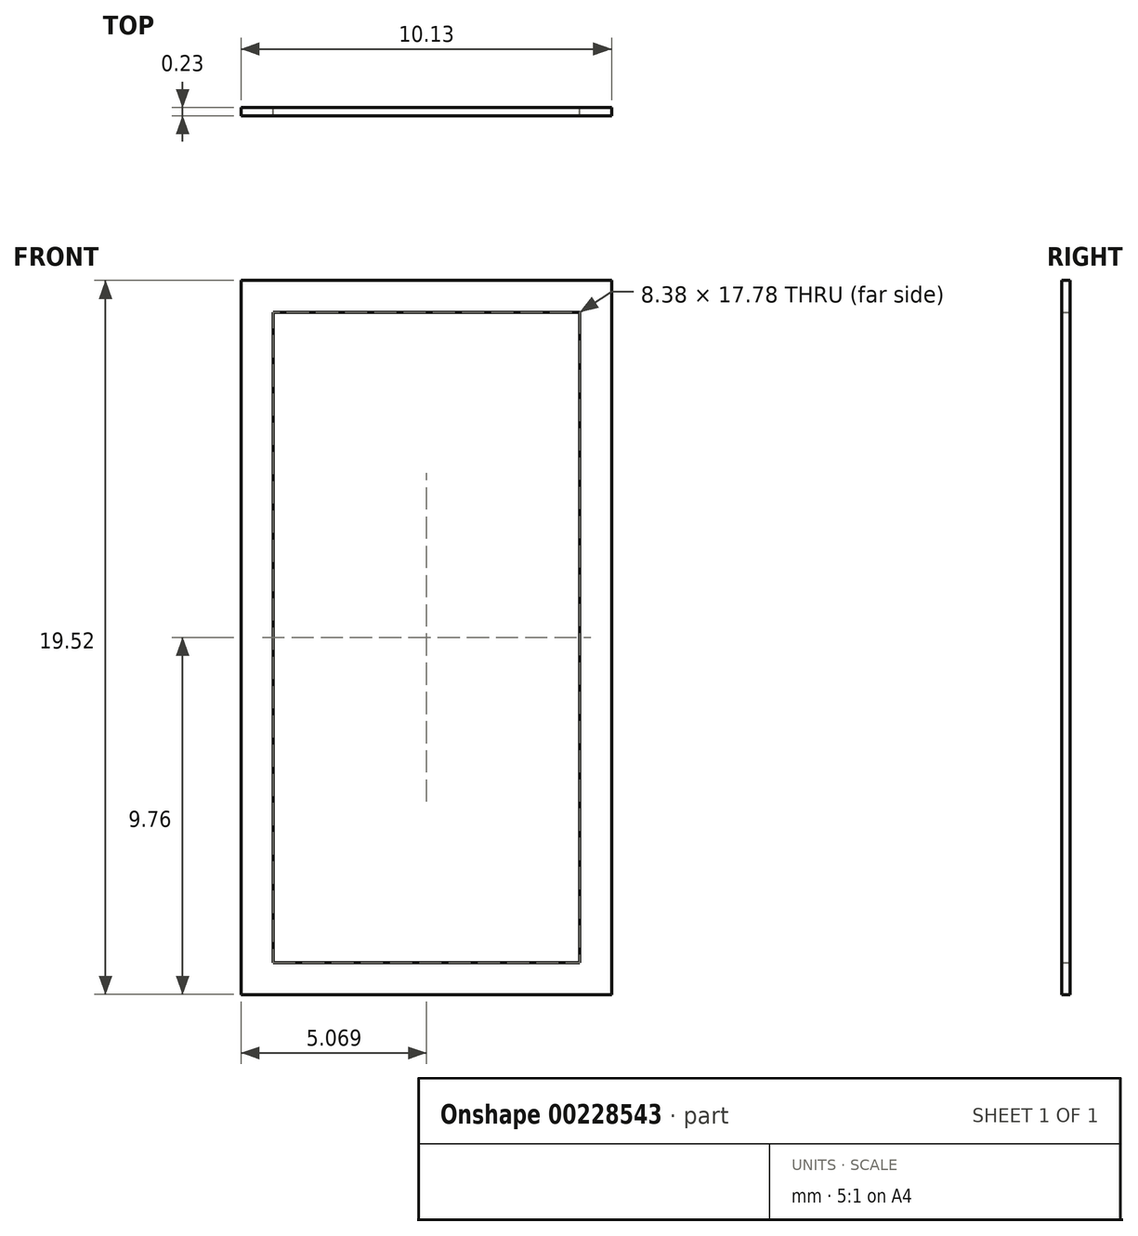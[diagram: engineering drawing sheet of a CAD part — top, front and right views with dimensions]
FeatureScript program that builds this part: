
annotation { "Feature Type Name" : "Feature", "Feature Type Description" : "" }
export const myFeature = defineFeature(function(context is Context, id is Id, definition is map)
    precondition{}
    {
        {
            var Q0;
            Q0=qCreatedBy(makeId("Front.planeOp"),FACE);
            var sketch = newSketch(context, id + "F0", { "sketchPlane" : qUnion([Q0])});
            skLineSegment(sketch, "E0.bottom", {"start": v(0, 0) * mm, "end": v(-8.38, 0) * mm});
            skLineSegment(sketch, "E0.top", {"start": v(0, 17.78) * mm, "end": v(-8.38, 17.78) * mm});
            skLineSegment(sketch, "E0.left", {"start": v(0, 0) * mm, "end": v(0, 17.78) * mm});
            skLineSegment(sketch, "E0.right", {"start": v(-8.38, 0) * mm, "end": v(-8.38, 17.78) * mm});
            skLineSegment(sketch, "E1.bottom", {"start": v(0.87, -0.87) * mm, "end": v(-9.26, -0.87) * mm});
            skLineSegment(sketch, "E1.top", {"start": v(0.87, 18.65) * mm, "end": v(-9.26, 18.65) * mm});
            skLineSegment(sketch, "E1.left", {"start": v(0.87, -0.87) * mm, "end": v(0.87, 18.65) * mm});
            skLineSegment(sketch, "E1.right", {"start": v(-9.26, -0.87) * mm, "end": v(-9.26, 18.65) * mm});
            skSolve(sketch);
        }
        {
            var Q0;
            Q0=makeQuery(id+"F0.imprint","IMPRINT",FACE,{"disambiguationData":[TD([[makeQuery(id+"F0.imprint","IMPRINT",EDGE,{"derivedFrom":sQuery(id+"F0.wireOp",EDGE,"E0.bottom")}),1.0]])]});
            extrude(context, id + "F1", {"entities" : qUnion([Q0]), "depth" : 0.23 * mm});
        }
    });
